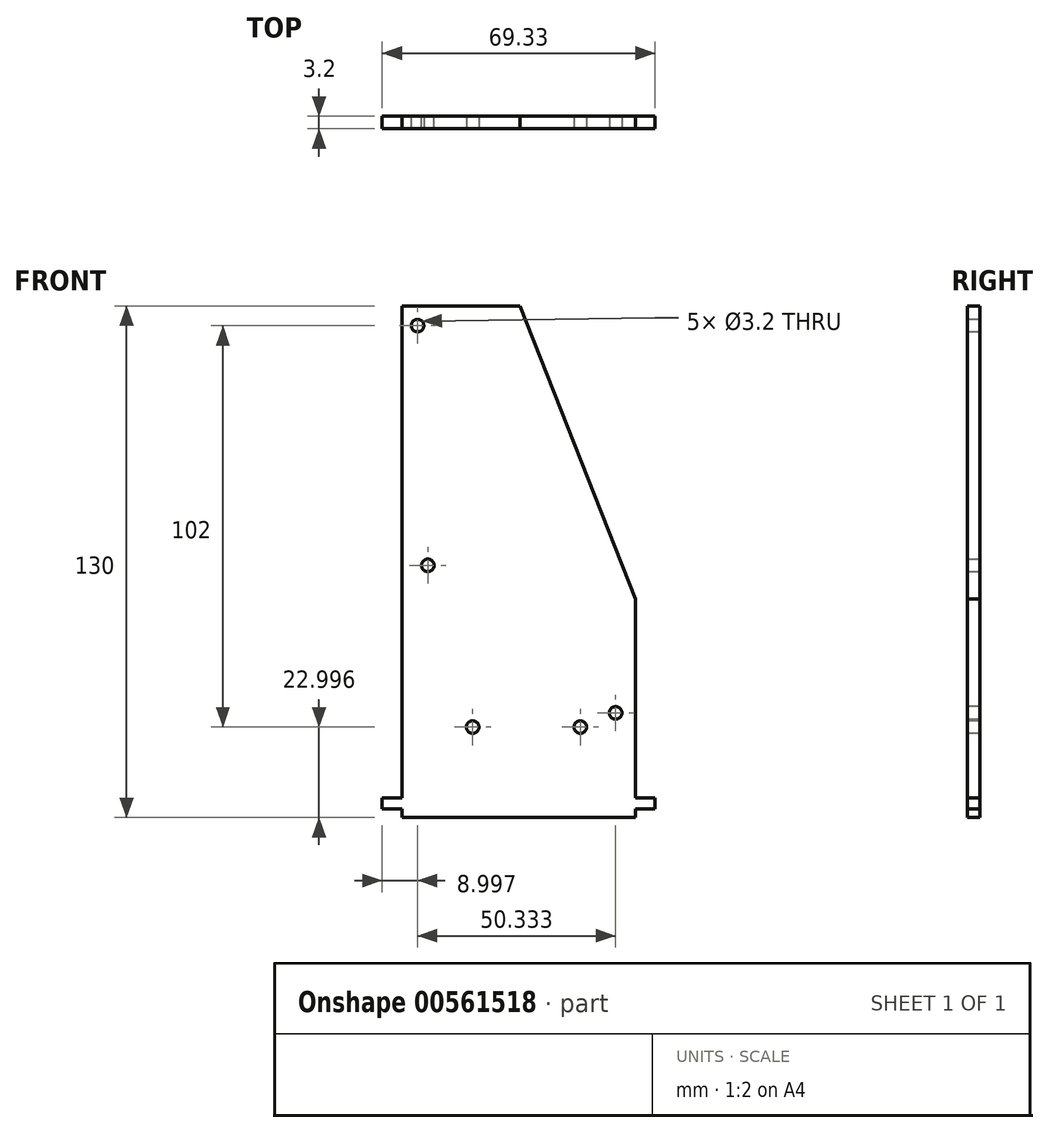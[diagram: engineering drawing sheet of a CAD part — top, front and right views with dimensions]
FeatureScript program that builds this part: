
annotation { "Feature Type Name" : "Feature", "Feature Type Description" : "" }
export const myFeature = defineFeature(function(context is Context, id is Id, definition is map)
    precondition{}
    {
        {
            var Q0;
            Q0=qCreatedBy(makeId("Front.planeOp"),FACE);
            var sketch = newSketch(context, id + "F0", { "sketchPlane" : qUnion([Q0])});
            skLineSegment(sketch, "E0.bottom", {"start": v(-42.53, 3.53) * mm, "end": v(16.8, 3.53) * mm});
            skLineSegment(sketch, "E0.left", {"start": v(-42.53, 3.53) * mm, "end": v(-42.53, -52.04) * mm});
            skLineSegment(sketch, "E0.right", {"start": v(16.8, 3.53) * mm, "end": v(16.8, -52.04) * mm});
            skLineSegment(sketch, "E1.bottom", {"start": v(-42.53, 77.96) * mm, "end": v(-12.53, 77.96) * mm});
            skLineSegment(sketch, "E1.top", {"start": v(-42.53, 30.53) * mm, "end": v(-12.53, 30.53) * mm});
            skLineSegment(sketch, "E1.left", {"start": v(-42.53, 77.96) * mm, "end": v(-42.53, 30.53) * mm});
            skLineSegment(sketch, "E1.right", {"start": v(-12.53, 77.96) * mm, "end": v(-12.53, 30.53) * mm});
            skLineSegment(sketch, "E2", {"start": v(-42.53, 77.96) * mm, "end": v(-42.53, -52.04) * mm});
            skLineSegment(sketch, "E3", {"start": v(-12.53, 77.96) * mm, "end": v(16.8, 3.53) * mm});
            skCircle(sketch, "E4", {"center": v(-35.93, 12.05) * mm, "radius": 1.6 * mm});
            skLineSegment(sketch, "E5", {"start": v(-42.53, -52.04) * mm, "end": v(16.8, -52.04) * mm});
            skSolve(sketch);
        }
        {
            var Q0;
            {var subQ1=sQuery(id+"F0.wireOp",EDGE,"E0.bottom");Q0=makeQuery(id+"F0.imprint","IMPRINT",FACE,{"disambiguationData":[TD([[makeQuery(id+"F0.imprint","IMPRINT",EDGE,{"derivedFrom":subQ1}),1.0]])]});}
            var Q1;
            {var subQ0=sQuery(id+"F0.wireOp",EDGE,"E1.bottom");Q1=makeQuery(id+"F0.imprint","IMPRINT",FACE,{"disambiguationData":[TD([[makeQuery(id+"F0.imprint","IMPRINT",EDGE,{"derivedFrom":subQ0}),-1.0]])]});}
            var Q2;
            {var subQ0=sQuery(id+"F0.wireOp",EDGE,"E0.bottom");Q2=makeQuery(id+"F0.imprint","IMPRINT",FACE,{"disambiguationData":[TD([[makeQuery(id+"F0.imprint","IMPRINT",EDGE,{"derivedFrom":subQ0}),-1.0]])]});}
            extrude(context, id + "F1", {"entities" : qUnion([Q0, Q1, Q2]), "depth" : 3.2 * mm, "offsetDistance" : 25 * mm});
        }
        {
            var Q0;
            Q0=qSketchRegion(id+"F0",true);
            extrude(context, id + "F2", {"entities" : qUnion([Q0]), "operationType" : NewBodyOperationType.ADD, "depth" : 2.3 * mm, "offsetDistance" : 25 * mm});
        }
        {
            var Q0;
            Q0=makeQuery(id+"F1.opExtrude","CAP_FACE",FACE,{"disambiguationData":[OSD([sQuery(id+"F0.wireOp",EDGE,"E0.right"),sQuery(id+"F0.wireOp",EDGE,"E1.bottom"),sQuery(id+"F0.wireOp",EDGE,"E2"),sQuery(id+"F0.wireOp",EDGE,"E3"),sQuery(id+"F0.wireOp",EDGE,"E4"),sQuery(id+"F0.wireOp",EDGE,"E5")])],"isStart":false});
            var sketch = newSketch(context, id + "F3", { "sketchPlane" : qUnion([Q0])});
            skCircle(sketch, "E6", {"center": v(11.8, -25.44) * mm, "radius": 1.6 * mm});
            skSolve(sketch);
        }
        {
            var Q0;
            Q0 = qSketchRegion(id + "F3", true);
            extrude(context, id + "F4", {"entities" : qUnion([Q0]), "operationType" : NewBodyOperationType.REMOVE, "oppositeDirection" : true, "depth" : 11 * mm, "offsetDistance" : 25 * mm});
        }
        {
            var Q0;
            Q0=makeQuery(id+"F1.opExtrude","CAP_FACE",FACE,{"disambiguationData":[OSD([sQuery(id+"F0.wireOp",EDGE,"E0.right"),sQuery(id+"F0.wireOp",EDGE,"E1.bottom"),sQuery(id+"F0.wireOp",EDGE,"E2"),sQuery(id+"F0.wireOp",EDGE,"E3"),sQuery(id+"F0.wireOp",EDGE,"E4"),sQuery(id+"F0.wireOp",EDGE,"E5")])],"isStart":false});
            var sketch = newSketch(context, id + "F5", { "sketchPlane" : qUnion([Q0])});
            skCircle(sketch, "E7", {"center": v(-38.53, 72.96) * mm, "radius": 1.6 * mm});
            skSolve(sketch);
        }
        {
            var Q0;
            Q0 = qSketchRegion(id + "F5", true);
            extrude(context, id + "F6", {"entities" : qUnion([Q0]), "operationType" : NewBodyOperationType.REMOVE, "oppositeDirection" : true, "depth" : 11 * mm, "offsetDistance" : 25 * mm});
        }
        {
            var Q0;
            Q0=makeQuery(id+"F1.opExtrude","SWEPT_FACE",FACE,{"disambiguationData":[OSD([sQuery(id+"F0.wireOp",EDGE,"E0.right")])]});
            var sketch = newSketch(context, id + "F7", { "sketchPlane" : qUnion([Q0])});
            skLineSegment(sketch, "E8", {"start": v(-3.2, -49.84) * mm, "end": v(0, -49.84) * mm});
            skLineSegment(sketch, "E9", {"start": v(0, -49.84) * mm, "end": v(0, -47.04) * mm});
            skLineSegment(sketch, "E10", {"start": v(0, -47.04) * mm, "end": v(-3.2, -47.04) * mm});
            skLineSegment(sketch, "E11", {"start": v(-3.2, -47.04) * mm, "end": v(-3.2, -49.84) * mm});
            skSolve(sketch);
        }
        {
            var Q0;
            Q0 = qSketchRegion(id + "F7", true);
            extrude(context, id + "F8", {"entities" : qUnion([Q0]), "operationType" : NewBodyOperationType.ADD, "depth" : 5 * mm, "offsetDistance" : 25 * mm});
        }
        {
            var Q0;
            Q0=makeQuery(id+"F1.opExtrude","SWEPT_FACE",FACE,{"disambiguationData":[OSD([sQuery(id+"F0.wireOp",EDGE,"E2")])]});
            var sketch = newSketch(context, id + "F9", { "sketchPlane" : qUnion([Q0])});
            skLineSegment(sketch, "E12", {"start": v(0, -47.04) * mm, "end": v(3.2, -47.04) * mm});
            skLineSegment(sketch, "E13", {"start": v(3.2, -47.04) * mm, "end": v(3.2, -49.84) * mm});
            skLineSegment(sketch, "E14", {"start": v(3.2, -49.84) * mm, "end": v(0, -49.84) * mm});
            skLineSegment(sketch, "E15", {"start": v(0, -49.84) * mm, "end": v(0, -47.04) * mm});
            skSolve(sketch);
        }
        {
            var Q0;
            Q0 = qSketchRegion(id + "F9", true);
            extrude(context, id + "F10", {"entities" : qUnion([Q0]), "operationType" : NewBodyOperationType.ADD, "depth" : 5 * mm, "offsetDistance" : 25 * mm});
        }
        {
            var Q0;
            Q0=makeQuery(id+"F10.boolean.opBoolean","MERGE",FACE,{"derivedFrom":[makeQuery(id+"F8.boolean.opBoolean","MERGE",FACE,{"derivedFrom":[makeQuery(id+"F1.opExtrude","CAP_FACE",FACE,{"disambiguationData":[OSD([sQuery(id+"F0.wireOp",EDGE,"E0.right"),sQuery(id+"F0.wireOp",EDGE,"E1.bottom"),sQuery(id+"F0.wireOp",EDGE,"E2"),sQuery(id+"F0.wireOp",EDGE,"E3"),sQuery(id+"F0.wireOp",EDGE,"E4"),sQuery(id+"F0.wireOp",EDGE,"E5")])],"isStart":false}),makeQuery(id+"F8.opExtrude","SWEPT_FACE",FACE,{"disambiguationData":[OSD([sQuery(id+"F7.wireOp",EDGE,"E11")])]})]}),makeQuery(id+"F10.opExtrude","SWEPT_FACE",FACE,{"disambiguationData":[OSD([sQuery(id+"F9.wireOp",EDGE,"E13")])]})]});
            var sketch = newSketch(context, id + "F11", { "sketchPlane" : qUnion([Q0])});
            skCircle(sketch, "E16", {"center": v(-24.53, -29.04) * mm, "radius": 1.6 * mm});
            skSolve(sketch);
        }
        {
            var Q0;
            Q0 = qSketchRegion(id + "F11", true);
            extrude(context, id + "F12", {"entities" : qUnion([Q0]), "operationType" : NewBodyOperationType.REMOVE, "oppositeDirection" : true, "depth" : 8 * mm, "offsetDistance" : 25 * mm});
        }
        {
            var Q0;
            Q0=makeQuery(id+"F10.boolean.opBoolean","MERGE",FACE,{"derivedFrom":[makeQuery(id+"F8.boolean.opBoolean","MERGE",FACE,{"derivedFrom":[makeQuery(id+"F1.opExtrude","CAP_FACE",FACE,{"disambiguationData":[OSD([sQuery(id+"F0.wireOp",EDGE,"E0.right"),sQuery(id+"F0.wireOp",EDGE,"E1.bottom"),sQuery(id+"F0.wireOp",EDGE,"E2"),sQuery(id+"F0.wireOp",EDGE,"E3"),sQuery(id+"F0.wireOp",EDGE,"E4"),sQuery(id+"F0.wireOp",EDGE,"E5")])],"isStart":false}),makeQuery(id+"F8.opExtrude","SWEPT_FACE",FACE,{"disambiguationData":[OSD([sQuery(id+"F7.wireOp",EDGE,"E11")])]})]}),makeQuery(id+"F10.opExtrude","SWEPT_FACE",FACE,{"disambiguationData":[OSD([sQuery(id+"F9.wireOp",EDGE,"E13")])]})]});
            var sketch = newSketch(context, id + "F13", { "sketchPlane" : qUnion([Q0])});
            skCircle(sketch, "E17", {"center": v(2.8, -29.04) * mm, "radius": 1.6 * mm});
            skSolve(sketch);
        }
        {
            var Q0;
            Q0 = qSketchRegion(id + "F13", true);
            extrude(context, id + "F14", {"entities" : qUnion([Q0]), "operationType" : NewBodyOperationType.REMOVE, "oppositeDirection" : true, "depth" : 10 * mm, "offsetDistance" : 25 * mm});
        }
    });
